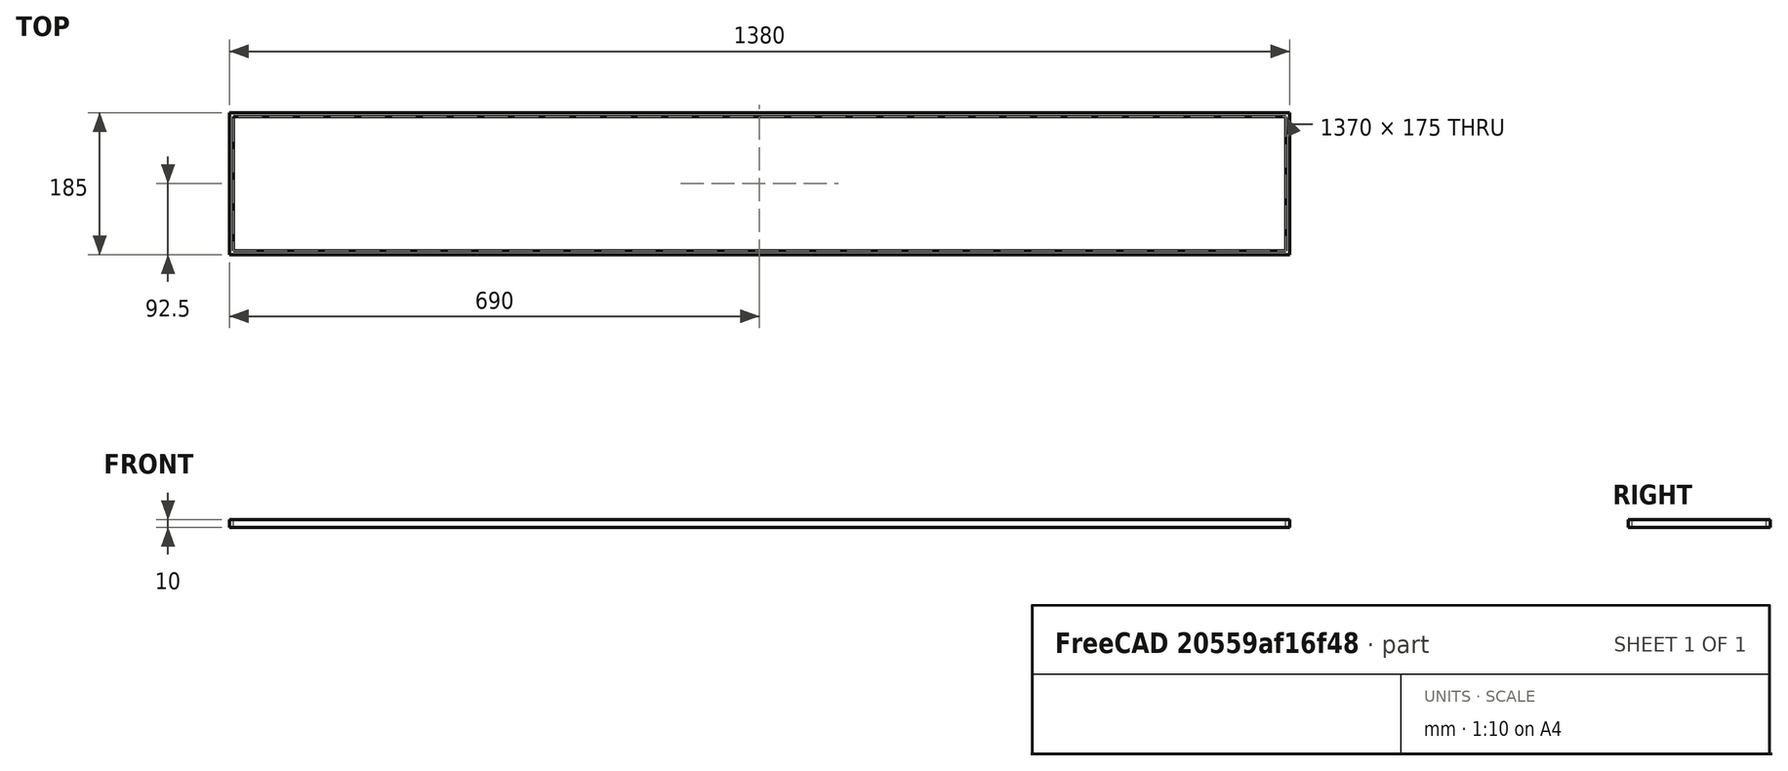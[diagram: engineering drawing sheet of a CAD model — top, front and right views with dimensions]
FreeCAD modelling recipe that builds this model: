
FCSTD DOCUMENT  (FreeCAD 0.19R24276 (Git))
Label: Parket_size_175x1370x10
License: All rights reserved
LicenseURL: http://en.wikipedia.org/wiki/All_rights_reserved
objects: Sketcher::SketchObject×1, PartDesign::Pad×1, PartDesign::Body×1
note: 4 computed .brp shape members not serialized (recipe doc carries the construction recipe); baked Part::Feature solids carry a one-line shape summary decoded from their .brp

FEATURE [Sketcher::SketchObject] Sketch
  FullyConstrained = true
  MapMode = 5
  Support = -> [XY_Plane]
  sketch-geometry (8):
    g0: LineSegment StartX=0 StartY=0 StartZ=0 EndX=1370 EndY=0 EndZ=0
    g1: LineSegment StartX=1370 StartY=0 StartZ=0 EndX=1370 EndY=175 EndZ=0
    g2: LineSegment StartX=1370 StartY=175 StartZ=0 EndX=0 EndY=175 EndZ=0
    g3: LineSegment StartX=0 StartY=175 StartZ=0 EndX=0 EndY=0 EndZ=0
    g4: LineSegment StartX=-5 StartY=-5 StartZ=0 EndX=1375 EndY=-5 EndZ=0
    g5: LineSegment StartX=1375 StartY=-5 StartZ=0 EndX=1375 EndY=180 EndZ=0
    g6: LineSegment StartX=1375 StartY=180 StartZ=0 EndX=-5 EndY=180 EndZ=0
    g7: LineSegment StartX=-5 StartY=180 StartZ=0 EndX=-5 EndY=-5 EndZ=0
  constraints (23):
    c: Coincident(g0,g1)
    c: Coincident(g1,g2)
    c: Coincident(g2,g3)
    c: Coincident(g3,g0)
    c: Horizontal(g0)
    c: Horizontal(g2)
    c: Vertical(g1)
    c: Vertical(g3)
    c: Coincident(g0,g-1)
    c: DistanceY(g3,g3) = 175
    c: DistanceX(g0,g0) = 1370
    c: Coincident(g4,g5)
    c: Coincident(g5,g6)
    c: Coincident(g6,g7)
    c: Coincident(g7,g4)
    c: Horizontal(g4)
    c: Horizontal(g6)
    c: Vertical(g5)
    c: Vertical(g7)
    c: DistanceX(g4,g0) = 5
    c: DistanceX(g0,g4) = 5
    c: DistanceY(g4,g0) = 5
    c: DistanceY(g1,g5) = 5
FEATURE [PartDesign::Pad] Pad
  Direction = (1,1,1)
  Length = 10
  Length2 = 100
  Profile = -> Sketch
  Type = 0
FEATURE [PartDesign::Body] Body
  Group = -> [Sketch,Pad]
  Origin = -> Origin
  Tip = -> Pad
